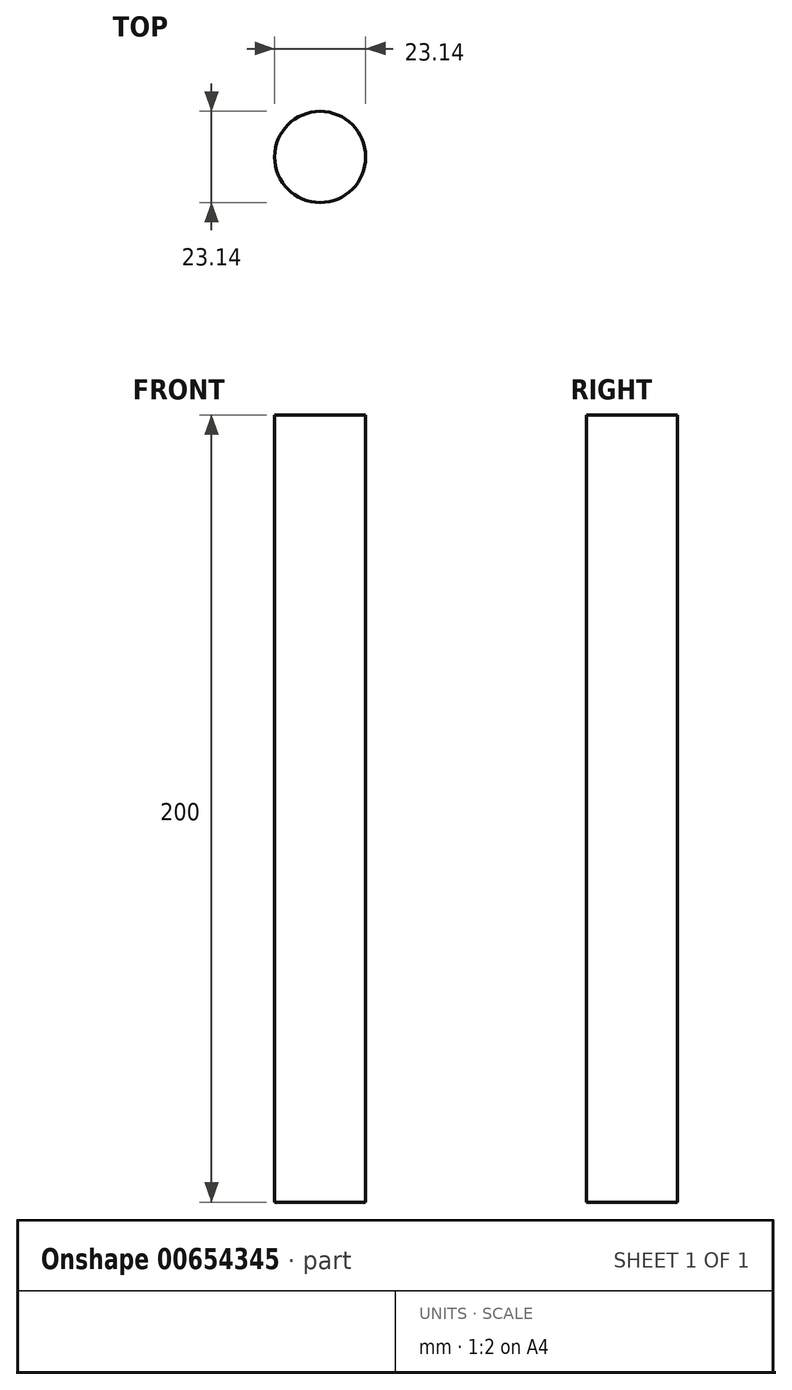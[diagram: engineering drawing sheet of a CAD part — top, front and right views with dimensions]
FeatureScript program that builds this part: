
annotation { "Feature Type Name" : "Feature", "Feature Type Description" : "" }
export const myFeature = defineFeature(function(context is Context, id is Id, definition is map)
    precondition{}
    {
        {
            var Q0;
            Q0=qCreatedBy(makeId("Top.planeOp"),FACE);
            var sketch = newSketch(context, id + "F0", { "sketchPlane" : qUnion([Q0])});
            skCircle(sketch, "E0", {"center": v(0, 0) * mm, "radius": 11.57 * mm});
            skSolve(sketch);
        }
        {
            var Q0;
            Q0=sQuery(id+"F0.wireOp",EDGE,"E0");
            extrude(context, id + "F1", {"bodyType" : ToolBodyType.SURFACE, "surfaceEntities" : qUnion([Q0]), "depth" : 200 * mm, "offsetDistance" : 25.4 * mm});
        }
    });
